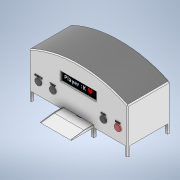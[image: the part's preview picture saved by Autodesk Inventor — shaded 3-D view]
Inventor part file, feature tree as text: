
AUTODESK INVENTOR PART (.ipt)
format: ipt  version: 2021 (Build 250183000, 183)  size: 1,127,424 bytes
history: native  units: mm
features: sketch x33, extrude x30, chamfer x3, fillet x2, other x2, plane x1
ambient origin geometry x8: Origin, YZ Plane, XZ Plane, XY Plane, X Axis, Y Axis, Z Axis, Center Point
bodies: Solid1 (feature_tree)
feature tree (71):
  extrude  "Extrusion1"  Depth=68.5mm
  extrude  "Extrusion2"  Depth=5.0mm
  extrude  "Extrusion3"  Depth=10.0mm TaperAngle=0.0deg
  extrude  "Extrusion4"  Depth=5.0mm
  extrude  "Extrusion5"  Depth=2.5mm
  extrude  "Extrusion6"  Depth=86.5mm
  extrude  "Extrusion7"  Depth=1.1mm
  extrude  "Extrusion8"  Depth=5.0mm TaperAngle=0.0deg
  extrude  "Extrusion9"  Depth=30.0mm TaperAngle=0.0deg
  extrude  "Extrusion13"  Depth=2.3mm
  extrude  "Extrusion14"  Depth=2.3mm
  fillet  "Fillet1"  Radius=50.0mm
  extrude  "Extrusion16"  Depth=68.5mm TaperAngle=0.0deg
  extrude  "Extrusion17"  Depth=1.0mm TaperAngle=0.0deg
  sketch  "Sketch23"  dims[d40=1.0mm d41=0.0mm d56=1.1mm]
  extrude  "Extrusion18"  Depth=1.0mm
  extrude  "Extrusion19"  Depth=20.0mm TaperAngle=0.0deg
  extrude  "Extrusion20"  Depth=10.0mm
  extrude  "Extrusion21"  Depth=10.0mm
  sketch  "Sketch29"  dims[d81=5.0mm d82=30.0mm d83=0.0mm]
  extrude  "Extrusion22"  Depth=5.0mm
  extrude  "Extrusion23"  Depth=30.0mm TaperAngle=0.0deg
  chamfer  "Chamfer1"  Distance=20.0mm
  extrude  "Extrusion25"  Depth=5.0mm
  extrude  "Extrusion26"  Depth=20.0mm TaperAngle=0.0deg
  extrude  "Extrusion27"  Depth=75.0mm TaperAngle=0.0deg
  extrude  "Extrusion28"  Depth=5.0mm
  fillet  "Fillet2"  Radius=5.0mm
  extrude  "Extrusion29"  Depth=5.0mm
  extrude  "Extrusion30"  Depth=20.0mm TaperAngle=0.0deg
  extrude  "Extrusion31"  Depth=5.0mm
  chamfer  "Chamfer2"  Distance=5.0mm
  chamfer  "Chamfer3"  Distance=30.0mm
  extrude  "Extrusion32"  Depth=2.5mm
  plane  "Work Plane1"
  other  "Decal1"
  extrude  "Extrusion33"  Depth=1.0mm TaperAngle=0.0deg
  extrude  "Extrusion34"  Depth=1.0mm
  extrude  "Extrusion35"  Depth=10.0mm
  sketch  "Sketch1"  dims[d0=94.0mm d1=68.5mm]
  sketch  "Sketch2"  dims[d2=4.0mm d3=0.0mm d4=5.0mm]
  sketch  "Sketch3"  dims[d5=10.0mm d6=5.0mm d7=0.0mm]
  sketch  "Sketch4"  dims[d8=5.0mm d9=5.0mm]
  sketch  "Sketch5"  dims[d11=2.5mm d12=2.5mm]
  sketch  "Sketch6"  dims[d13=2.5mm d15=86.5mm]
  sketch  "Sketch8"  dims[d16=5.0mm d17=0.0mm d19=1.1mm]
  sketch  "Sketch10"  dims[d20=1.1mm d21=5.0mm d22=0.0mm]
  sketch  "Sketch11"  dims[d23=2.5mm d24=30.0mm d25=0.0mm]
  sketch  "Sketch15"  dims[d26=2.3mm d27=2.3mm]
  sketch  "Sketch17"  dims[d28=2.3mm d29=2.3mm d30=50.0mm d31=0.0mm]
  sketch  "Sketch19"  dims[d32=20.0mm d34=68.5mm d35=0.0mm]
  sketch  "Sketch21"  dims[d37=1.1mm d38=1.0mm d39=0.0mm]
  sketch  "Sketch24"  dims[d57=94.0mm d58=0.0mm d69=20.0mm d70=0.0mm]
  sketch  "Sketch25"  dims[d75=10.0mm d76=2.3mm]
  sketch  "Sketch26"  dims[d77=10.0mm d78=5.0mm]
  sketch  "Sketch28"  dims[d79=20.0mm d80=5.0mm]
  sketch  "Sketch30"  dims[d84=5.0mm]
  sketch  "Sketch32"  dims[d85=5.0mm d90=20.0mm d91=0.0mm]
  sketch  "Sketch34"  dims[d94=5.0mm d95=5.0mm]
  sketch  "Sketch35"  dims[d96=5.0mm d97=20.0mm d98=0.0mm]
  sketch  "Sketch36"  dims[d99=75.0mm d100=0.0mm d101=75.0mm d102=0.0mm]
  sketch  "Sketch37"  dims[d103=5.0mm d104=5.0mm d105=5.0mm]
  sketch  "Sketch38"  dims[d106=5.0mm d107=5.0mm]
  sketch  "Sketch39"  dims[d108=5.0mm d109=20.0mm d110=0.0mm]
  sketch  "Sketch40"  dims[d111=5.0mm d112=5.0mm]
  sketch  "Sketch41"  dims[d113=5.0mm]
  sketch  "Sketch43"  dims[d114=5.0mm]
  other  "Image1"
  sketch  "Sketch44"  dims[d115=5.0mm d116=5.0mm d117=0.0mm d120=30.0mm d121=0.0mm]
  sketch  "Sketch45"  dims[d126=2.0mm d127=2.0mm d128=45.0deg d129=2.5mm]
  sketch  "Sketch46"  dims[d130=68.0mm d131=0.0mm d132=68.0mm d133=0.0mm d134=25.0mm d135=10.0mm d136=42.117007mm d137=26.15mm d138=25.0mm d139=42.117007mm d140=26.15mm d141=2.5mm d142=0.0mm d143=5.0mm d144=20.0mm d145=20.0mm d146=0.0mm d147=10.0mm d148=5.0mm d149=5.0mm d150=5.0mm d151=0.0mm d153=2.3mm d154=2.3mm d155=2.3mm d156=40.0mm d157=0.0mm d158=250.0mm d159=94.0mm d160=0.0mm d161=2.0mm d162=2.0mm d163=45.0deg d164=2.0mm d165=2.0mm d166=45.0deg d170=40.0mm d171=20.0mm d172=40.0mm d173=20.0mm d174=2.2mm d175=0.0mm d176=30.25mm d185=26.15mm d186=26.15mm d187=25.0mm d189=15.0mm d190=15.0mm d191=15.0mm d192=15.0mm d193=2.2mm d194=0.0mm d195=14.0mm d196=14.0mm d197=14.0mm d198=14.0mm d199=4.0mm d200=0.0mm d202=1.0mm d203=0.0mm d71=0.5mm d72=0.872665mm]
